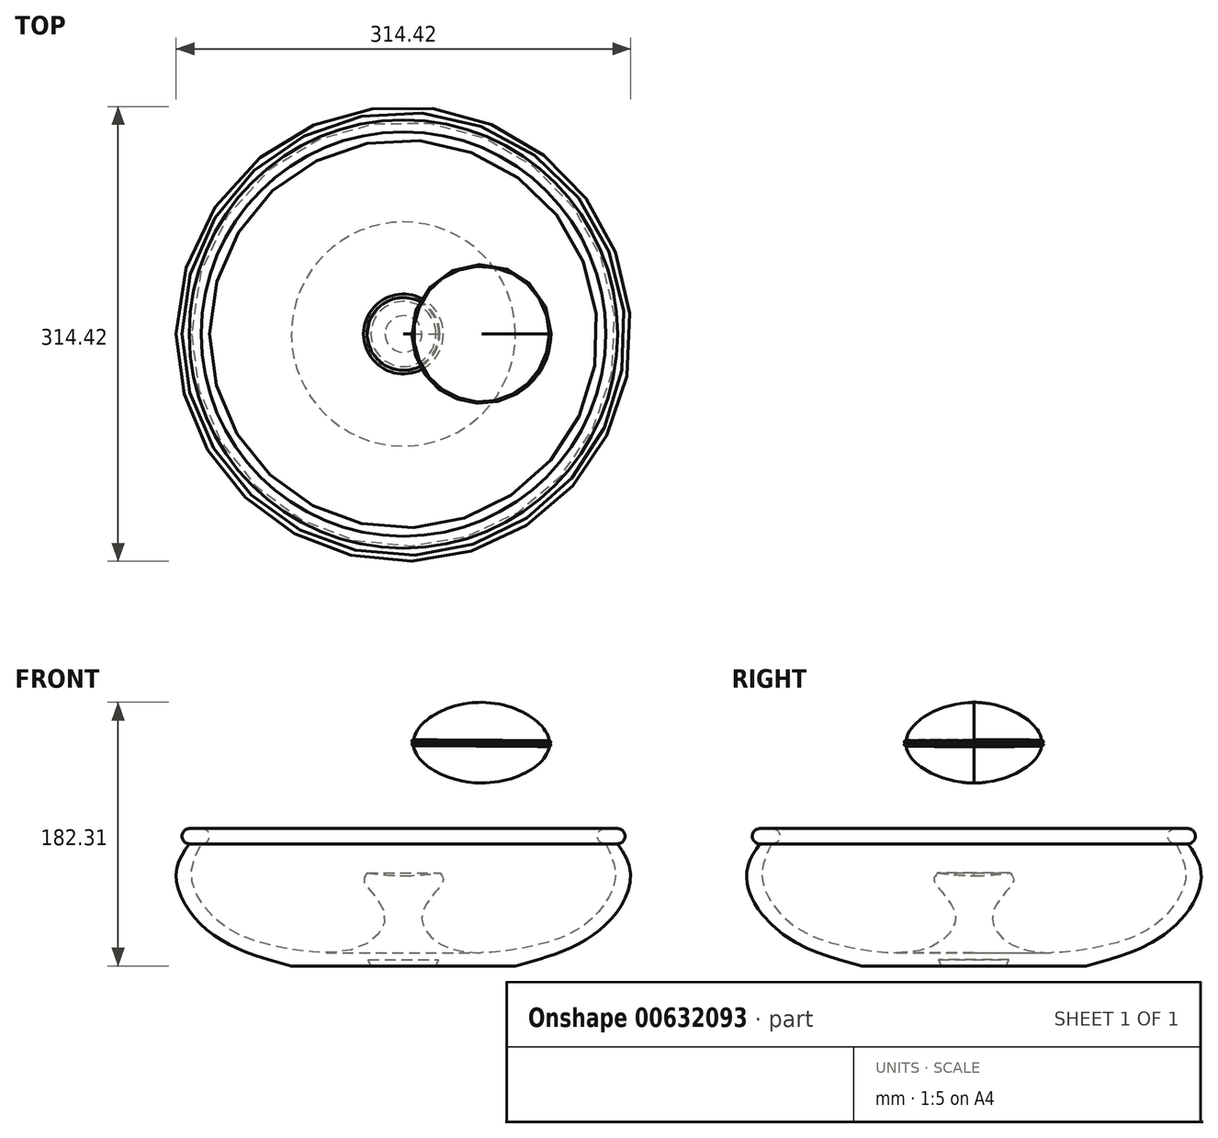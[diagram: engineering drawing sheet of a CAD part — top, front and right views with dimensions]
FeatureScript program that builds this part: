
annotation { "Feature Type Name" : "Feature", "Feature Type Description" : "" }
export const myFeature = defineFeature(function(context is Context, id is Id, definition is map)
    precondition{}
    {
        {
            var Q0;
            Q0=qCreatedBy(makeId("Front.planeOp"),FACE);
            var sketch = newSketch(context, id + "F0", { "sketchPlane" : qUnion([Q0])});
            skLineSegment(sketch, "E0", {"start": v(0, 4.22) * mm, "end": v(24.39, 4.22) * mm});
            skLineSegment(sketch, "E1", {"start": v(24.39, 4.22) * mm, "end": v(22.48, 0) * mm});
            skLineSegment(sketch, "E2", {"start": v(22.48, 0) * mm, "end": v(77.46, 0) * mm});
            skLineSegment(sketch, "E3", {"start": v(0, -7.02) * mm, "end": v(77.46, -7.02) * mm, "construction": true});
            skLineSegment(sketch, "E4", {"start": v(0, 0) * mm, "end": v(0, 95) * mm, "construction": true});
            skLineSegment(sketch, "E5", {"start": v(-7.06, 0) * mm, "end": v(-7.06, 64.37) * mm, "construction": true});
            skLineSegment(sketch, "E6", {"start": v(-7.06, 64.37) * mm, "end": v(157.14, 64.37) * mm, "construction": true});
            skLineSegment(sketch, "E7", {"start": v(0, 95) * mm, "end": v(152.71, 95) * mm, "construction": true});
            skLineSegment(sketch, "E8", {"start": v(0, 62.36) * mm, "end": v(24.96, 62.36) * mm, "construction": true});
            skFitSpline(sketch, "E9", {"points": [v(77.46, 0) * mm, v(118.75, 13.92) * mm, v(147.69, 37.43) * mm, v(157.14, 64.37) * mm, v(148.1, 84.46) * mm], "startDerivative": vector(162.34, 45.7) * mm, "endDerivative": vector(-63.82, 92.91) * mm});
            skFitSpline(sketch, "E10", {"points": [v(0, 62.36) * mm, v(25.17, 64.37) * mm, v(24.96, 64.37) * mm], "startDerivative": vector(33.23, 0) * mm, "endDerivative": vector(-5.43, -0.13) * mm});
            skFitSpline(sketch, "E11", {"points": [v(25.17, 64.37) * mm, v(27.46, 60.63) * mm, v(25.17, 54.82) * mm, v(12.79, 34.64) * mm, v(30.47, 12.89) * mm, v(89.14, 13.73) * mm, v(127.5, 30.22) * mm, v(146.12, 58.21) * mm, v(139.87, 84.46) * mm], "startDerivative": vector(46.32, -76.04) * mm, "endDerivative": vector(-115.7, 241.7) * mm});
            skLineSegment(sketch, "E12", {"start": v(0, 62.36) * mm, "end": v(0, 4.22) * mm});
            skArc(sketch, "E13", {"start": v(148.1, 84.46) * mm, "mid": v(153.2, 89.73) * mm, "end": v(148.1, 95) * mm});
            skArc(sketch, "E14", {"start": v(139.87, 95) * mm, "mid": v(134.1, 89.73) * mm, "end": v(139.87, 84.46) * mm});
            skLineSegment(sketch, "E15", {"start": v(139.87, 95) * mm, "end": v(148.1, 95) * mm});
            skSolve(sketch);
        }
        {
            var Q0;
            Q0=qCreatedBy(makeId("Front.planeOp"),FACE);
            var sketch = newSketch(context, id + "F1", { "sketchPlane" : qUnion([Q0])});
            skLineSegment(sketch, "E16", {"start": v(6.41, 155.11) * mm, "end": v(100.95, 153.69) * mm});
            skPoint(sketch, "E17", {"position": v(100.8, 155.67) * mm});
            skPoint(sketch, "E18", {"position": v(6.43, 155.67) * mm});
            skArc(sketch, "E19", {"start": v(100.95, 153.69) * mm, "mid": v(101.97, 154.76) * mm, "end": v(100.8, 155.67) * mm});
            skArc(sketch, "E20", {"start": v(100.8, 151.73) * mm, "mid": v(101.92, 152.62) * mm, "end": v(100.95, 153.69) * mm});
            skLineSegment(sketch, "E21", {"start": v(54.1, 182.3) * mm, "end": v(53.68, 126.49) * mm});
            skFitSpline(sketch, "E22", {"points": [v(54.1, 182.3) * mm, v(100.95, 153.69) * mm, v(53.68, 126.49) * mm], "startDerivative": vector(149.16, -2.44) * mm, "endDerivative": vector(-152.19, 0) * mm});
            skSolve(sketch);
        }
        {
            var Q0;
            {var subQ0=sQuery(id+"F1.wireOp",EDGE,"E22");var subQ4=sQuery(id+"F1.wireOp",EDGE,"E21");var subQ6=makeQuery(id+"F1.imprint","INTERSECT",VERTEX,{"disambiguationData":[OD(1.0)],"derivedFrom":[subQ4,subQ0]});Q0=makeQuery(id+"F1.imprint","IMPRINT",FACE,{"disambiguationData":[TD([[makeQuery(id+"F1.imprint","IMPRINT",EDGE,{"disambiguationData":[TD([[subQ6,1.0]])],"derivedFrom":subQ4}),1.0]])]});}
            var Q1;
            {var subQ0=sQuery(id+"F1.wireOp",EDGE,"E22");var subQ4=sQuery(id+"F1.wireOp",EDGE,"E21");var subQ6=makeQuery(id+"F1.imprint","INTERSECT",VERTEX,{"disambiguationData":[OD(0.0)],"derivedFrom":[subQ4,subQ0]});Q1=makeQuery(id+"F1.imprint","IMPRINT",FACE,{"disambiguationData":[TD([[makeQuery(id+"F1.imprint","IMPRINT",EDGE,{"disambiguationData":[TD([[subQ6,-1.0]])],"derivedFrom":subQ4}),1.0]])]});}
            var Q2;
            {var subQ0=sQuery(id+"F1.wireOp",EDGE,"E22");var subQ1=sQuery(id+"F1.wireOp",EDGE,"E20");var subQ3=makeQuery(id+"F1.imprint","INTERSECT",VERTEX,{"derivedFrom":[subQ1,subQ0]});Q2=makeQuery(id+"F1.imprint","IMPRINT",FACE,{"disambiguationData":[TD([[makeQuery(id+"F1.imprint","IMPRINT",EDGE,{"disambiguationData":[TD([[subQ3,-1.0]])],"derivedFrom":subQ1}),1.0]])]});}
            var Q3;
            {var subQ0=sQuery(id+"F1.wireOp",EDGE,"E22");var subQ1=sQuery(id+"F1.wireOp",EDGE,"E19");var subQ3=makeQuery(id+"F1.imprint","INTERSECT",VERTEX,{"derivedFrom":[subQ1,subQ0]});Q3=makeQuery(id+"F1.imprint","IMPRINT",FACE,{"disambiguationData":[TD([[makeQuery(id+"F1.imprint","IMPRINT",EDGE,{"disambiguationData":[TD([[subQ3,1.0]])],"derivedFrom":subQ1}),1.0]])]});}
            var Q4;
            Q4=sQuery(id+"F1.wireOp",EDGE,"E21");
            revolve(context, id + "F2", {"entities" : qUnion([Q0, Q1, Q2, Q3]), "axis" : qUnion([Q4]), "revolveType" : RevolveType.FULL});
        }
        {
            var Q0;
            Q0=makeQuery(id+"F0.imprint","IMPRINT",FACE,{"disambiguationData":[TD([[makeQuery(id+"F0.imprint","IMPRINT",EDGE,{"derivedFrom":sQuery(id+"F0.wireOp",EDGE,"E0")}),1.0]])]});
            var Q1;
            Q1=sQuery(id+"F0.wireOp",EDGE,"E4");
            revolve(context, id + "F3", {"entities" : qUnion([Q0]), "axis" : qUnion([Q1]), "revolveType" : RevolveType.FULL});
        }
    });
